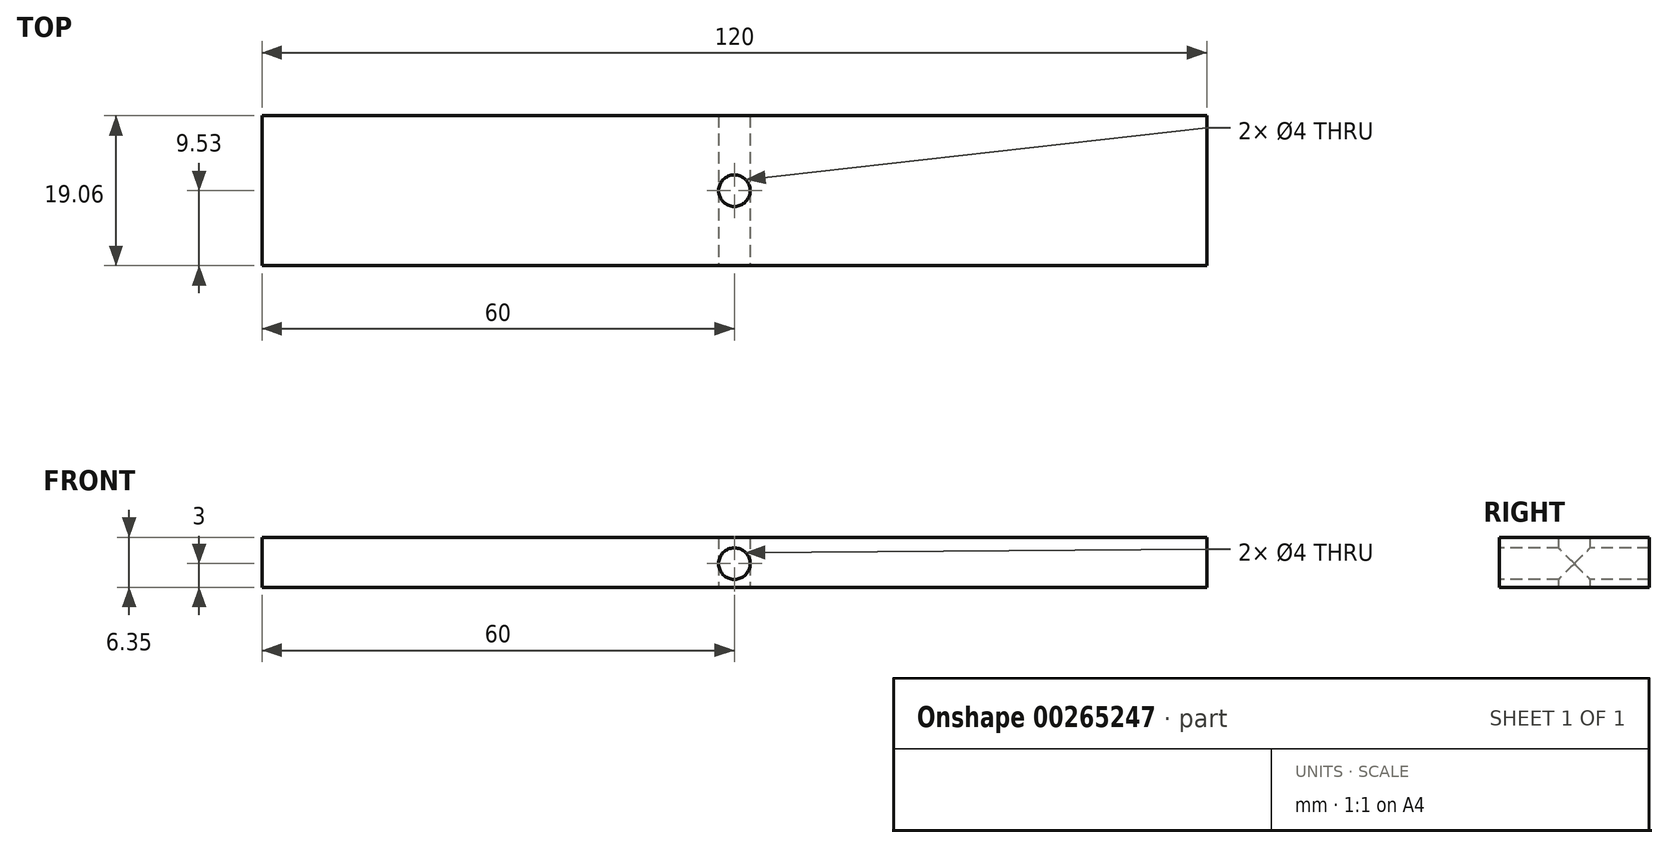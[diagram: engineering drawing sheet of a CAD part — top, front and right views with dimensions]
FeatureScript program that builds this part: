
annotation { "Feature Type Name" : "Feature", "Feature Type Description" : "" }
export const myFeature = defineFeature(function(context is Context, id is Id, definition is map)
    precondition{}
    {
        {
            var Q0;
            Q0=qCreatedBy(makeId("Top.planeOp"),FACE);
            var sketch = newSketch(context, id + "F0", { "sketchPlane" : qUnion([Q0])});
            skLineSegment(sketch, "E0.bottom", {"start": v(60, -9.52) * mm, "end": v(-60, -9.53) * mm});
            skLineSegment(sketch, "E0.top", {"start": v(60, 9.53) * mm, "end": v(-60, 9.52) * mm});
            skLineSegment(sketch, "E0.left", {"start": v(60, -9.52) * mm, "end": v(60, 9.53) * mm});
            skLineSegment(sketch, "E0.right", {"start": v(-60, -9.53) * mm, "end": v(-60, 9.52) * mm});
            skPoint(sketch, "E0.middle", {"position": v(0, 0) * mm});
            skCircle(sketch, "E1", {"center": v(0, 0) * mm, "radius": 2 * mm});
            skLineSegment(sketch, "E2.bottom", {"start": v(5, -9.52) * mm, "end": v(-5, -9.53) * mm});
            skLineSegment(sketch, "E2.top", {"start": v(5, 9.53) * mm, "end": v(-5, 9.52) * mm});
            skLineSegment(sketch, "E2.left", {"start": v(5, -9.52) * mm, "end": v(5, 9.53) * mm});
            skLineSegment(sketch, "E2.right", {"start": v(-5, -9.53) * mm, "end": v(-5, 9.52) * mm});
            skSolve(sketch);
        }
        {
            var Q0;
            Q0=qSketchRegion(id+"F0",true);
            extrude(context, id + "F1", {"entities" : qUnion([Q0]), "depth" : 6.35 * mm});
        }
        {
            var Q0;
            Q0=makeQuery(id+"F1.opExtrude","SWEPT_FACE",FACE,{"disambiguationData":[OSD([sQuery(id+"F0.wireOp",EDGE,"E0.bottom"),sQuery(id+"F0.wireOp",EDGE,"E2.bottom")])]});
            var sketch = newSketch(context, id + "F2", { "sketchPlane" : qUnion([Q0])});
            skCircle(sketch, "E3", {"center": v(0, 3) * mm, "radius": 2 * mm});
            skSolve(sketch);
        }
        {
            var Q0;
            Q0=qSketchRegion(id+"F2",true);
            extrude(context, id + "F3", {"entities" : qUnion([Q0]), "operationType" : NewBodyOperationType.REMOVE, "endBound" : BoundingType.THROUGH_ALL, "oppositeDirection" : true, "depth" : 30 * mm});
        }
    });
